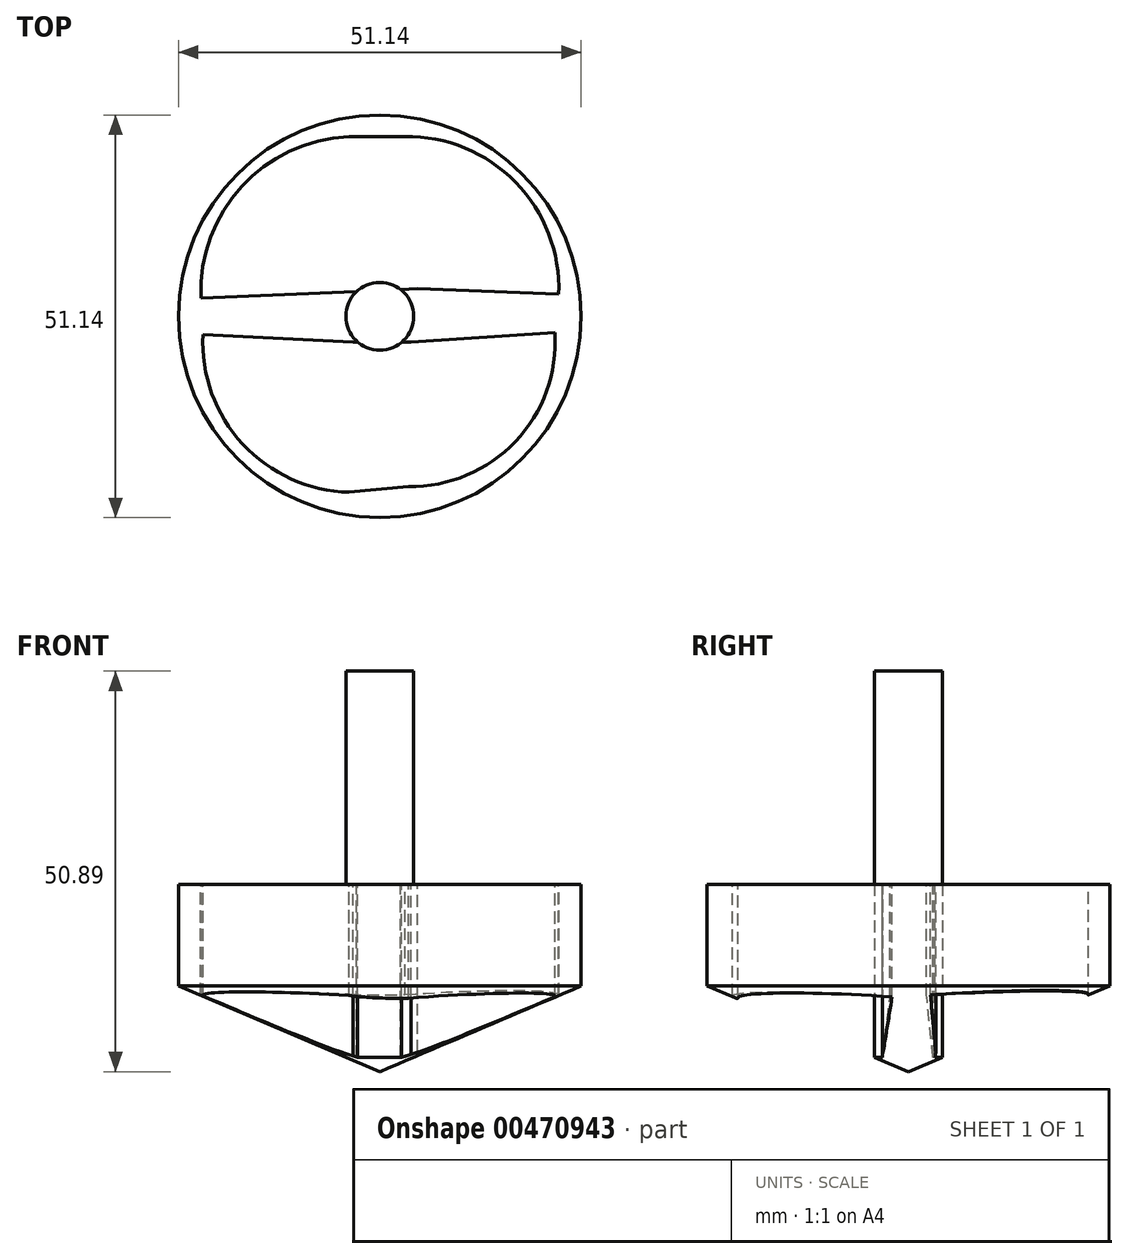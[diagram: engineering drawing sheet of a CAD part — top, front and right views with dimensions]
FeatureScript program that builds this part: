
annotation { "Feature Type Name" : "Feature", "Feature Type Description" : "" }
export const myFeature = defineFeature(function(context is Context, id is Id, definition is map)
    precondition{}
    {
        {
            var Q0;
            Q0=qCreatedBy(makeId("Front.planeOp"),FACE);
            var sketch = newSketch(context, id + "F0", { "sketchPlane" : qUnion([Q0])});
            skLineSegment(sketch, "E0", {"start": v(0, 0) * mm, "end": v(25.57, 10.89) * mm});
            skLineSegment(sketch, "E1", {"start": v(25.57, 10.89) * mm, "end": v(25.57, 23.8) * mm});
            skLineSegment(sketch, "E2", {"start": v(0, 0) * mm, "end": v(0, 50.9) * mm});
            skLineSegment(sketch, "E3", {"start": v(0, 50.9) * mm, "end": v(4.3, 50.9) * mm});
            skLineSegment(sketch, "E4", {"start": v(4.3, 50.9) * mm, "end": v(4.3, 23.8) * mm});
            skLineSegment(sketch, "E5", {"start": v(4.3, 23.8) * mm, "end": v(25.57, 23.8) * mm});
            skSolve(sketch);
        }
        {
            var Q0;
            Q0=makeQuery(id+"F0.imprint","IMPRINT",FACE,{"disambiguationData":[TD([[makeQuery(id+"F0.imprint","IMPRINT",EDGE,{"derivedFrom":sQuery(id+"F0.wireOp",EDGE,"E0")}),1.0]])]});
            var Q1;
            Q1=sQuery(id+"F0.wireOp",EDGE,"E2");
            revolve(context, id + "F1", {"entities" : qUnion([Q0]), "axis" : qUnion([Q1]), "revolveType" : RevolveType.FULL});
        }
        {
            var Q0;
            Q0=makeQuery(id+"F1.opRevolve","SWEPT_FACE",FACE,{"disambiguationData":[OSD([sQuery(id+"F0.wireOp",EDGE,"E5")])]});
            var sketch = newSketch(context, id + "F2", { "sketchPlane" : qUnion([Q0])});
            skArc(sketch, "E6", {"start": v(-3.9, 22.84) * mm, "mid": v(-17.55, 16.47) * mm, "end": v(-22.72, 2.32) * mm});
            skArc(sketch, "E7", {"start": v(22.72, 2.8) * mm, "mid": v(17.25, 17.02) * mm, "end": v(3.18, 22.84) * mm});
            skArc(sketch, "E8", {"start": v(-22.48, -2.32) * mm, "mid": v(-17.4, -16.24) * mm, "end": v(-3.9, -22.35) * mm});
            skArc(sketch, "E9", {"start": v(3.66, -21.62) * mm, "mid": v(17.23, -15.92) * mm, "end": v(22.23, -2.08) * mm});
            skLineSegment(sketch, "E10", {"start": v(-3.9, 22.84) * mm, "end": v(-3.01, 3.14) * mm});
            skLineSegment(sketch, "E11", {"start": v(-22.72, 2.32) * mm, "end": v(-3.01, 3.14) * mm});
            skLineSegment(sketch, "E12", {"start": v(3.18, 22.84) * mm, "end": v(3.44, 3.55) * mm});
            skLineSegment(sketch, "E13", {"start": v(3.44, 3.55) * mm, "end": v(22.72, 2.8) * mm});
            skLineSegment(sketch, "E14", {"start": v(3.94, -3.29) * mm, "end": v(22.23, -2.08) * mm});
            skLineSegment(sketch, "E15", {"start": v(3.94, -3.29) * mm, "end": v(3.66, -21.62) * mm});
            skLineSegment(sketch, "E16", {"start": v(-3.4, -3.26) * mm, "end": v(-3.9, -22.35) * mm});
            skLineSegment(sketch, "E17", {"start": v(-22.48, -2.32) * mm, "end": v(-3.4, -3.26) * mm});
            skSolve(sketch);
        }
        {
            var Q0;
            Q0=makeQuery(id+"F2.imprint","IMPRINT",FACE,{"disambiguationData":[TD([[makeQuery(id+"F2.imprint","IMPRINT",EDGE,{"derivedFrom":sQuery(id+"F2.wireOp",EDGE,"E6")}),1.0]])]});
            var Q1;
            Q1=makeQuery(id+"F2.imprint","IMPRINT",FACE,{"disambiguationData":[TD([[makeQuery(id+"F2.imprint","IMPRINT",EDGE,{"derivedFrom":sQuery(id+"F2.wireOp",EDGE,"E7")}),1.0]])]});
            var Q2;
            Q2=makeQuery(id+"F2.imprint","IMPRINT",FACE,{"disambiguationData":[TD([[makeQuery(id+"F2.imprint","IMPRINT",EDGE,{"derivedFrom":sQuery(id+"F2.wireOp",EDGE,"E9")}),1.0]])]});
            var Q3;
            Q3=makeQuery(id+"F2.imprint","IMPRINT",FACE,{"disambiguationData":[TD([[makeQuery(id+"F2.imprint","IMPRINT",EDGE,{"derivedFrom":sQuery(id+"F2.wireOp",EDGE,"E8")}),1.0]])]});
            extrude(context, id + "F3", {"entities" : qUnion([Q0, Q1, Q2, Q3]), "operationType" : NewBodyOperationType.REMOVE, "oppositeDirection" : true, "depth" : 25.4 * mm});
        }
        {
            var Q0;
            Q0=makeQuery(id+"F1.opRevolve","SWEPT_FACE",FACE,{"disambiguationData":[OSD([sQuery(id+"F0.wireOp",EDGE,"E5")])]});
            var sketch = newSketch(context, id + "F4", { "sketchPlane" : qUnion([Q0])});
            skLineSegment(sketch, "E18", {"start": v(-3.01, 3.14) * mm, "end": v(4.81, 3.5) * mm});
            skLineSegment(sketch, "E19", {"start": v(4.81, 3.5) * mm, "end": v(3.18, 22.84) * mm});
            skLineSegment(sketch, "E20", {"start": v(3.18, 22.84) * mm, "end": v(-3.9, 22.84) * mm});
            skLineSegment(sketch, "E21", {"start": v(-3.9, 22.84) * mm, "end": v(-3.01, 3.14) * mm});
            skSolve(sketch);
        }
        {
            var Q0;
            Q0=makeQuery(id+"F4.imprint","IMPRINT",FACE,{"disambiguationData":[TD([[makeQuery(id+"F4.imprint","IMPRINT",EDGE,{"derivedFrom":sQuery(id+"F4.wireOp",EDGE,"E20")}),1.0]])]});
            extrude(context, id + "F5", {"entities" : qUnion([Q0]), "operationType" : NewBodyOperationType.REMOVE, "oppositeDirection" : true, "depth" : 25.4 * mm});
        }
        {
            var Q0;
            Q0=makeQuery(id+"F1.opRevolve","SWEPT_FACE",FACE,{"disambiguationData":[OSD([sQuery(id+"F0.wireOp",EDGE,"E5")])]});
            var sketch = newSketch(context, id + "F6", { "sketchPlane" : qUnion([Q0])});
            skLineSegment(sketch, "E22", {"start": v(0.2, -7.38) * mm, "end": v(3.66, -21.62) * mm});
            skPoint(sketch, "E22.startSnap0", {"position": v(0.2, -4.3) * mm});
            skLineSegment(sketch, "E23", {"start": v(3.66, -21.62) * mm, "end": v(-3.9, -22.35) * mm});
            skLineSegment(sketch, "E24", {"start": v(-3.9, -22.35) * mm, "end": v(-3.4, -3.26) * mm});
            skLineSegment(sketch, "E25", {"start": v(-3.4, -3.26) * mm, "end": v(3.94, -3.29) * mm});
            skLineSegment(sketch, "E26", {"start": v(3.94, -3.29) * mm, "end": v(3.66, -21.62) * mm});
            skSolve(sketch);
        }
        {
            var Q0;
            Q0=makeQuery(id+"F6.imprint","IMPRINT",FACE,{"disambiguationData":[TD([[makeQuery(id+"F6.imprint","IMPRINT",EDGE,{"derivedFrom":sQuery(id+"F6.wireOp",EDGE,"E23")}),-1.0]])]});
            extrude(context, id + "F7", {"entities" : qUnion([Q0]), "operationType" : NewBodyOperationType.REMOVE, "oppositeDirection" : true, "depth" : 25.4 * mm});
        }
    });
